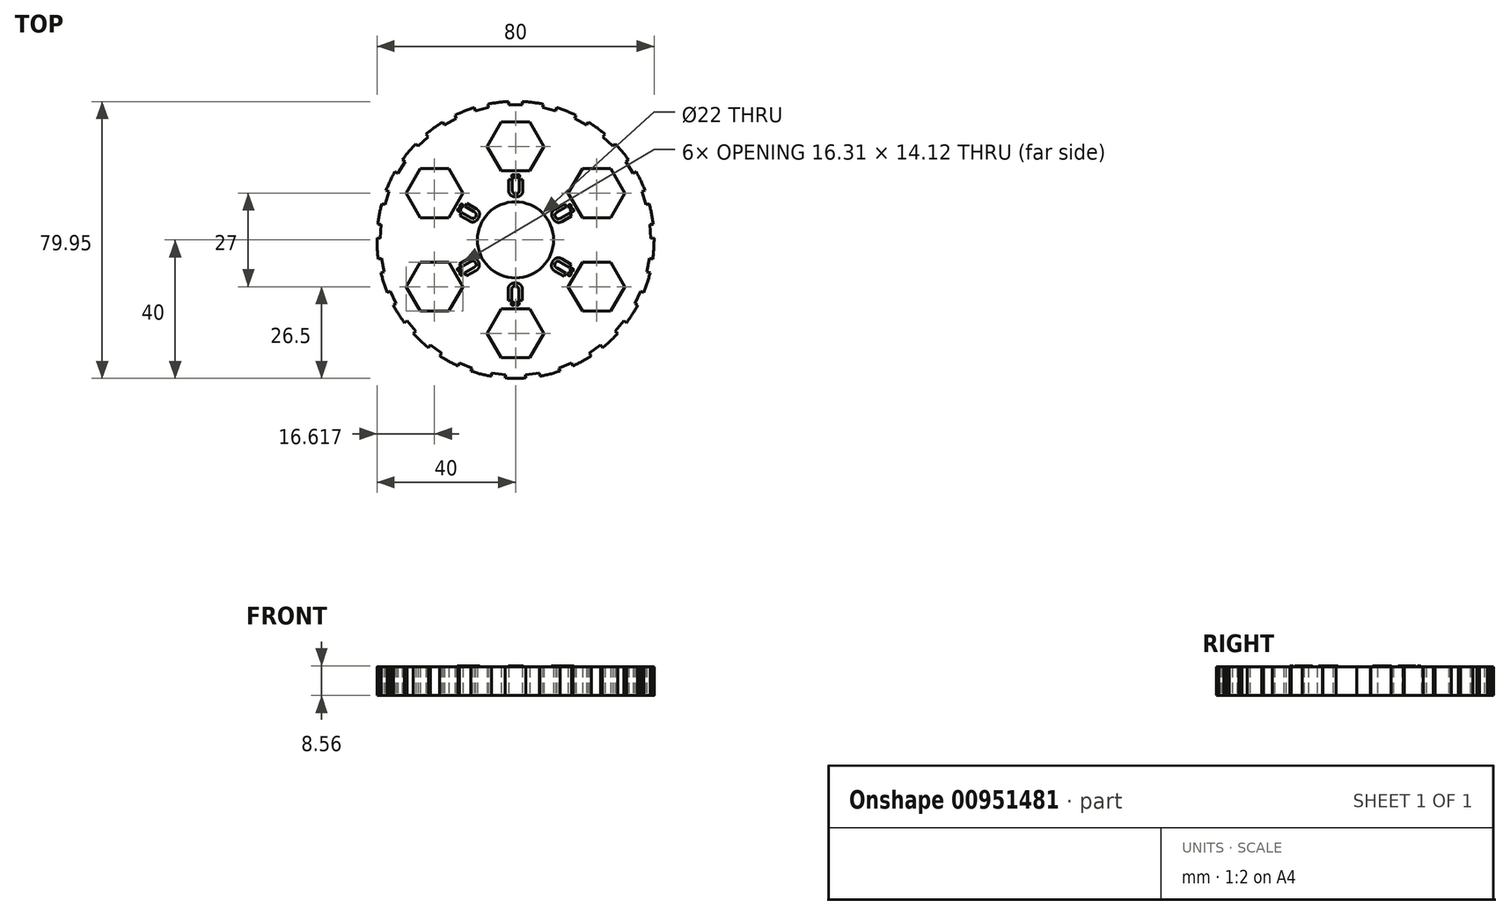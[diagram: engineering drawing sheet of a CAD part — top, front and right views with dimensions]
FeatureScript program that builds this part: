
annotation { "Feature Type Name" : "Feature", "Feature Type Description" : "" }
export const myFeature = defineFeature(function(context is Context, id is Id, definition is map)
    precondition{}
    {
        {
            var Q0;
            Q0=qCreatedBy(makeId("Top.planeOp"),FACE);
            var sketch = newSketch(context, id + "F0", { "sketchPlane" : qUnion([Q0])});
            skCircle(sketch, "E0", {"center": v(0, 0) * mm, "radius": 11 * mm});
            skCircle(sketch, "E1", {"center": v(0, 0) * mm, "radius": 40 * mm});
            skCircle(sketch, "E2.cCircle", {"center": v(0, 27) * mm, "radius": 7.06 * mm, "construction": true});
            skLineSegment(sketch, "E2.0", {"start": v(8.15, 27) * mm, "end": v(4.08, 19.94) * mm});
            skLineSegment(sketch, "E2.1", {"start": v(4.08, 19.94) * mm, "end": v(-4.08, 19.94) * mm});
            skLineSegment(sketch, "E2.2", {"start": v(-4.08, 19.94) * mm, "end": v(-8.15, 27) * mm});
            skLineSegment(sketch, "E2.3", {"start": v(-8.15, 27) * mm, "end": v(-4.08, 34.06) * mm});
            skLineSegment(sketch, "E2.4", {"start": v(-4.08, 34.06) * mm, "end": v(4.08, 34.06) * mm});
            skLineSegment(sketch, "E2.5", {"start": v(4.08, 34.06) * mm, "end": v(8.15, 27) * mm});
            skPoint(sketch, "E2.0.midPoint", {"position": v(6.12, 23.47) * mm});
            skLineSegment(sketch, "E3.1.0", {"start": v(-15.23, 13.5) * mm, "end": v(-19.3, 6.44) * mm});
            skLineSegment(sketch, "E3.1.1", {"start": v(-31.54, 13.5) * mm, "end": v(-27.46, 20.56) * mm});
            skLineSegment(sketch, "E3.1.2", {"start": v(-19.3, 6.44) * mm, "end": v(-27.46, 6.44) * mm});
            skLineSegment(sketch, "E3.1.3", {"start": v(-27.46, 20.56) * mm, "end": v(-19.3, 20.56) * mm});
            skLineSegment(sketch, "E3.1.4", {"start": v(-27.46, 6.44) * mm, "end": v(-31.54, 13.5) * mm});
            skLineSegment(sketch, "E3.1.5", {"start": v(-19.3, 20.56) * mm, "end": v(-15.23, 13.5) * mm});
            skPoint(sketch, "E3.1.6", {"position": v(-17.27, 17.03) * mm});
            skCircle(sketch, "E3.1.7", {"center": v(-23.38, 13.5) * mm, "radius": 7.06 * mm, "construction": true});
            skLineSegment(sketch, "E3.2.0", {"start": v(-19.3, -6.44) * mm, "end": v(-15.23, -13.5) * mm});
            skLineSegment(sketch, "E3.2.1", {"start": v(-27.46, -20.56) * mm, "end": v(-31.54, -13.5) * mm});
            skLineSegment(sketch, "E3.2.2", {"start": v(-15.23, -13.5) * mm, "end": v(-19.3, -20.56) * mm});
            skLineSegment(sketch, "E3.2.3", {"start": v(-31.54, -13.5) * mm, "end": v(-27.46, -6.44) * mm});
            skLineSegment(sketch, "E3.2.4", {"start": v(-19.3, -20.56) * mm, "end": v(-27.46, -20.56) * mm});
            skLineSegment(sketch, "E3.2.5", {"start": v(-27.46, -6.44) * mm, "end": v(-19.3, -6.44) * mm});
            skPoint(sketch, "E3.2.6", {"position": v(-23.38, -6.44) * mm});
            skCircle(sketch, "E3.2.7", {"center": v(-23.38, -13.5) * mm, "radius": 7.06 * mm, "construction": true});
            skLineSegment(sketch, "E3.3.0", {"start": v(-4.08, -19.94) * mm, "end": v(4.08, -19.94) * mm});
            skLineSegment(sketch, "E3.3.1", {"start": v(4.08, -34.06) * mm, "end": v(-4.08, -34.06) * mm});
            skLineSegment(sketch, "E3.3.2", {"start": v(4.08, -19.94) * mm, "end": v(8.15, -27) * mm});
            skLineSegment(sketch, "E3.3.3", {"start": v(-4.08, -34.06) * mm, "end": v(-8.15, -27) * mm});
            skLineSegment(sketch, "E3.3.4", {"start": v(8.15, -27) * mm, "end": v(4.08, -34.06) * mm});
            skLineSegment(sketch, "E3.3.5", {"start": v(-8.15, -27) * mm, "end": v(-4.08, -19.94) * mm});
            skPoint(sketch, "E3.3.6", {"position": v(-6.12, -23.47) * mm});
            skCircle(sketch, "E3.3.7", {"center": v(0, -27) * mm, "radius": 7.06 * mm, "construction": true});
            skLineSegment(sketch, "E3.4.0", {"start": v(15.23, -13.5) * mm, "end": v(19.3, -6.44) * mm});
            skLineSegment(sketch, "E3.4.1", {"start": v(31.54, -13.5) * mm, "end": v(27.46, -20.56) * mm});
            skLineSegment(sketch, "E3.4.2", {"start": v(19.3, -6.44) * mm, "end": v(27.46, -6.44) * mm});
            skLineSegment(sketch, "E3.4.3", {"start": v(27.46, -20.56) * mm, "end": v(19.3, -20.56) * mm});
            skLineSegment(sketch, "E3.4.4", {"start": v(27.46, -6.44) * mm, "end": v(31.54, -13.5) * mm});
            skLineSegment(sketch, "E3.4.5", {"start": v(19.3, -20.56) * mm, "end": v(15.23, -13.5) * mm});
            skPoint(sketch, "E3.4.6", {"position": v(17.27, -17.03) * mm});
            skCircle(sketch, "E3.4.7", {"center": v(23.38, -13.5) * mm, "radius": 7.06 * mm, "construction": true});
            skLineSegment(sketch, "E3.5.0", {"start": v(19.3, 6.44) * mm, "end": v(15.23, 13.5) * mm});
            skLineSegment(sketch, "E3.5.1", {"start": v(27.46, 20.56) * mm, "end": v(31.54, 13.5) * mm});
            skLineSegment(sketch, "E3.5.2", {"start": v(15.23, 13.5) * mm, "end": v(19.3, 20.56) * mm});
            skLineSegment(sketch, "E3.5.3", {"start": v(31.54, 13.5) * mm, "end": v(27.46, 6.44) * mm});
            skLineSegment(sketch, "E3.5.4", {"start": v(19.3, 20.56) * mm, "end": v(27.46, 20.56) * mm});
            skLineSegment(sketch, "E3.5.5", {"start": v(27.46, 6.44) * mm, "end": v(19.3, 6.44) * mm});
            skPoint(sketch, "E3.5.6", {"position": v(23.38, 6.44) * mm});
            skCircle(sketch, "E3.5.7", {"center": v(23.38, 13.5) * mm, "radius": 7.06 * mm, "construction": true});
            skLineSegment(sketch, "E4.bottom", {"start": v(2, 39) * mm, "end": v(-2, 39) * mm});
            skLineSegment(sketch, "E4.top", {"start": v(2, 41) * mm, "end": v(-2, 41) * mm});
            skLineSegment(sketch, "E4.left", {"start": v(2, 39) * mm, "end": v(2, 41) * mm});
            skLineSegment(sketch, "E4.right", {"start": v(-2, 39) * mm, "end": v(-2, 41) * mm});
            skPoint(sketch, "E4.middle", {"position": v(0, 40) * mm});
            skPoint(sketch, "E5.1.0", {"position": v(-9.95, 38.74) * mm});
            skLineSegment(sketch, "E5.1.1", {"start": v(-7.76, 38.27) * mm, "end": v(-11.64, 37.28) * mm});
            skLineSegment(sketch, "E5.1.2", {"start": v(-11.64, 37.28) * mm, "end": v(-12.13, 39.21) * mm});
            skLineSegment(sketch, "E5.1.3", {"start": v(-7.76, 38.27) * mm, "end": v(-8.26, 40.2) * mm});
            skLineSegment(sketch, "E5.1.4", {"start": v(-8.26, 40.2) * mm, "end": v(-12.13, 39.21) * mm});
            skPoint(sketch, "E5.2.0", {"position": v(-19.27, 35.05) * mm});
            skLineSegment(sketch, "E5.2.1", {"start": v(-17.04, 35.14) * mm, "end": v(-20.54, 33.21) * mm});
            skLineSegment(sketch, "E5.2.2", {"start": v(-20.54, 33.21) * mm, "end": v(-21.5, 34.97) * mm});
            skLineSegment(sketch, "E5.2.3", {"start": v(-17.04, 35.14) * mm, "end": v(-18, 36.9) * mm});
            skLineSegment(sketch, "E5.2.4", {"start": v(-18, 36.9) * mm, "end": v(-21.5, 34.97) * mm});
            skPoint(sketch, "E5.3.0", {"position": v(-27.38, 29.16) * mm});
            skLineSegment(sketch, "E5.3.1", {"start": v(-25.24, 29.8) * mm, "end": v(-28.16, 27.06) * mm});
            skLineSegment(sketch, "E5.3.2", {"start": v(-28.16, 27.06) * mm, "end": v(-29.52, 28.52) * mm});
            skLineSegment(sketch, "E5.3.3", {"start": v(-25.24, 29.8) * mm, "end": v(-26.6, 31.26) * mm});
            skLineSegment(sketch, "E5.3.4", {"start": v(-26.6, 31.26) * mm, "end": v(-29.52, 28.52) * mm});
            skPoint(sketch, "E5.4.0", {"position": v(-33.77, 21.43) * mm});
            skLineSegment(sketch, "E5.4.1", {"start": v(-31.86, 22.59) * mm, "end": v(-34, 19.2) * mm});
            skLineSegment(sketch, "E5.4.2", {"start": v(-34, 19.2) * mm, "end": v(-35.69, 20.28) * mm});
            skLineSegment(sketch, "E5.4.3", {"start": v(-31.86, 22.59) * mm, "end": v(-33.55, 23.66) * mm});
            skLineSegment(sketch, "E5.4.4", {"start": v(-33.55, 23.66) * mm, "end": v(-35.69, 20.28) * mm});
            skPoint(sketch, "E5.5.0", {"position": v(-38.04, 12.36) * mm});
            skLineSegment(sketch, "E5.5.1", {"start": v(-36.47, 13.95) * mm, "end": v(-37.7, 10.15) * mm});
            skLineSegment(sketch, "E5.5.2", {"start": v(-37.7, 10.15) * mm, "end": v(-39.61, 10.77) * mm});
            skLineSegment(sketch, "E5.5.3", {"start": v(-36.47, 13.95) * mm, "end": v(-38.38, 14.57) * mm});
            skLineSegment(sketch, "E5.5.4", {"start": v(-38.38, 14.57) * mm, "end": v(-39.61, 10.77) * mm});
            skPoint(sketch, "E5.6.0", {"position": v(-39.92, 2.51) * mm});
            skLineSegment(sketch, "E5.6.1", {"start": v(-38.8, 4.44) * mm, "end": v(-39.05, 0.45) * mm});
            skLineSegment(sketch, "E5.6.2", {"start": v(-39.05, 0.45) * mm, "end": v(-41.04, 0.58) * mm});
            skLineSegment(sketch, "E5.6.3", {"start": v(-38.8, 4.44) * mm, "end": v(-40.8, 4.57) * mm});
            skLineSegment(sketch, "E5.6.4", {"start": v(-40.8, 4.57) * mm, "end": v(-41.04, 0.58) * mm});
            skPoint(sketch, "E5.7.0", {"position": v(-39.3, -7.5) * mm});
            skLineSegment(sketch, "E5.7.1", {"start": v(-38.68, -5.34) * mm, "end": v(-37.93, -9.27) * mm});
            skLineSegment(sketch, "E5.7.2", {"start": v(-37.93, -9.27) * mm, "end": v(-39.9, -9.65) * mm});
            skLineSegment(sketch, "E5.7.3", {"start": v(-38.68, -5.34) * mm, "end": v(-40.65, -5.72) * mm});
            skLineSegment(sketch, "E5.7.4", {"start": v(-40.65, -5.72) * mm, "end": v(-39.9, -9.65) * mm});
            skPoint(sketch, "E5.8.0", {"position": v(-36.2, -17.03) * mm});
            skLineSegment(sketch, "E5.8.1", {"start": v(-36.14, -14.8) * mm, "end": v(-34.44, -18.42) * mm});
            skLineSegment(sketch, "E5.8.2", {"start": v(-34.44, -18.42) * mm, "end": v(-36.25, -19.27) * mm});
            skLineSegment(sketch, "E5.8.3", {"start": v(-36.14, -14.8) * mm, "end": v(-37.95, -15.65) * mm});
            skLineSegment(sketch, "E5.8.4", {"start": v(-37.95, -15.65) * mm, "end": v(-36.25, -19.27) * mm});
            skPoint(sketch, "E5.9.0", {"position": v(-30.82, -25.5) * mm});
            skLineSegment(sketch, "E5.9.1", {"start": v(-31.32, -23.32) * mm, "end": v(-28.78, -26.4) * mm});
            skLineSegment(sketch, "E5.9.2", {"start": v(-28.78, -26.4) * mm, "end": v(-30.32, -27.68) * mm});
            skLineSegment(sketch, "E5.9.3", {"start": v(-31.32, -23.32) * mm, "end": v(-32.87, -24.6) * mm});
            skLineSegment(sketch, "E5.9.4", {"start": v(-32.87, -24.6) * mm, "end": v(-30.32, -27.68) * mm});
            skPoint(sketch, "E5.10.0", {"position": v(-23.51, -32.36) * mm});
            skLineSegment(sketch, "E5.10.1", {"start": v(-24.54, -30.38) * mm, "end": v(-21.3, -32.73) * mm});
            skLineSegment(sketch, "E5.10.2", {"start": v(-21.3, -32.73) * mm, "end": v(-22.48, -34.35) * mm});
            skLineSegment(sketch, "E5.10.3", {"start": v(-24.54, -30.38) * mm, "end": v(-25.72, -32) * mm});
            skLineSegment(sketch, "E5.10.4", {"start": v(-25.72, -32) * mm, "end": v(-22.48, -34.35) * mm});
            skPoint(sketch, "E5.11.0", {"position": v(-14.72, -37.2) * mm});
            skLineSegment(sketch, "E5.11.1", {"start": v(-16.22, -35.53) * mm, "end": v(-12.5, -37) * mm});
            skLineSegment(sketch, "E5.11.2", {"start": v(-12.5, -37) * mm, "end": v(-13.23, -38.86) * mm});
            skLineSegment(sketch, "E5.11.3", {"start": v(-16.22, -35.53) * mm, "end": v(-16.95, -37.38) * mm});
            skLineSegment(sketch, "E5.11.4", {"start": v(-16.95, -37.38) * mm, "end": v(-13.23, -38.86) * mm});
            skPoint(sketch, "E5.12.0", {"position": v(-5.01, -39.68) * mm});
            skLineSegment(sketch, "E5.12.1", {"start": v(-6.87, -38.44) * mm, "end": v(-2.9, -38.94) * mm});
            skLineSegment(sketch, "E5.12.2", {"start": v(-2.9, -38.94) * mm, "end": v(-3.15, -40.93) * mm});
            skLineSegment(sketch, "E5.12.3", {"start": v(-6.87, -38.44) * mm, "end": v(-7.12, -40.43) * mm});
            skLineSegment(sketch, "E5.12.4", {"start": v(-7.12, -40.43) * mm, "end": v(-3.15, -40.93) * mm});
            skPoint(sketch, "E5.13.0", {"position": v(5.01, -39.68) * mm});
            skLineSegment(sketch, "E5.13.1", {"start": v(2.9, -38.94) * mm, "end": v(6.87, -38.44) * mm});
            skLineSegment(sketch, "E5.13.2", {"start": v(6.87, -38.44) * mm, "end": v(7.12, -40.43) * mm});
            skLineSegment(sketch, "E5.13.3", {"start": v(2.9, -38.94) * mm, "end": v(3.15, -40.93) * mm});
            skLineSegment(sketch, "E5.13.4", {"start": v(3.15, -40.93) * mm, "end": v(7.12, -40.43) * mm});
            skPoint(sketch, "E5.14.0", {"position": v(14.72, -37.2) * mm});
            skLineSegment(sketch, "E5.14.1", {"start": v(12.5, -37) * mm, "end": v(16.22, -35.53) * mm});
            skLineSegment(sketch, "E5.14.2", {"start": v(16.22, -35.53) * mm, "end": v(16.95, -37.38) * mm});
            skLineSegment(sketch, "E5.14.3", {"start": v(12.5, -37) * mm, "end": v(13.23, -38.86) * mm});
            skLineSegment(sketch, "E5.14.4", {"start": v(13.23, -38.86) * mm, "end": v(16.95, -37.38) * mm});
            skPoint(sketch, "E5.15.0", {"position": v(23.51, -32.36) * mm});
            skLineSegment(sketch, "E5.15.1", {"start": v(21.3, -32.73) * mm, "end": v(24.54, -30.38) * mm});
            skLineSegment(sketch, "E5.15.2", {"start": v(24.54, -30.38) * mm, "end": v(25.72, -32) * mm});
            skLineSegment(sketch, "E5.15.3", {"start": v(21.3, -32.73) * mm, "end": v(22.48, -34.35) * mm});
            skLineSegment(sketch, "E5.15.4", {"start": v(22.48, -34.35) * mm, "end": v(25.72, -32) * mm});
            skPoint(sketch, "E5.16.0", {"position": v(30.82, -25.5) * mm});
            skLineSegment(sketch, "E5.16.1", {"start": v(28.78, -26.4) * mm, "end": v(31.32, -23.32) * mm});
            skLineSegment(sketch, "E5.16.2", {"start": v(31.32, -23.32) * mm, "end": v(32.87, -24.6) * mm});
            skLineSegment(sketch, "E5.16.3", {"start": v(28.78, -26.4) * mm, "end": v(30.32, -27.68) * mm});
            skLineSegment(sketch, "E5.16.4", {"start": v(30.32, -27.68) * mm, "end": v(32.87, -24.6) * mm});
            skPoint(sketch, "E5.17.0", {"position": v(36.2, -17.03) * mm});
            skLineSegment(sketch, "E5.17.1", {"start": v(34.44, -18.42) * mm, "end": v(36.14, -14.8) * mm});
            skLineSegment(sketch, "E5.17.2", {"start": v(36.14, -14.8) * mm, "end": v(37.95, -15.65) * mm});
            skLineSegment(sketch, "E5.17.3", {"start": v(34.44, -18.42) * mm, "end": v(36.25, -19.27) * mm});
            skLineSegment(sketch, "E5.17.4", {"start": v(36.25, -19.27) * mm, "end": v(37.95, -15.65) * mm});
            skPoint(sketch, "E5.18.0", {"position": v(39.3, -7.5) * mm});
            skLineSegment(sketch, "E5.18.1", {"start": v(37.93, -9.27) * mm, "end": v(38.68, -5.34) * mm});
            skLineSegment(sketch, "E5.18.2", {"start": v(38.68, -5.34) * mm, "end": v(40.65, -5.72) * mm});
            skLineSegment(sketch, "E5.18.3", {"start": v(37.93, -9.27) * mm, "end": v(39.9, -9.65) * mm});
            skLineSegment(sketch, "E5.18.4", {"start": v(39.9, -9.65) * mm, "end": v(40.65, -5.72) * mm});
            skPoint(sketch, "E5.19.0", {"position": v(39.92, 2.51) * mm});
            skLineSegment(sketch, "E5.19.1", {"start": v(39.05, 0.45) * mm, "end": v(38.8, 4.44) * mm});
            skLineSegment(sketch, "E5.19.2", {"start": v(38.8, 4.44) * mm, "end": v(40.8, 4.57) * mm});
            skLineSegment(sketch, "E5.19.3", {"start": v(39.05, 0.45) * mm, "end": v(41.04, 0.58) * mm});
            skLineSegment(sketch, "E5.19.4", {"start": v(41.04, 0.58) * mm, "end": v(40.8, 4.57) * mm});
            skPoint(sketch, "E5.20.0", {"position": v(38.04, 12.36) * mm});
            skLineSegment(sketch, "E5.20.1", {"start": v(37.7, 10.15) * mm, "end": v(36.47, 13.95) * mm});
            skLineSegment(sketch, "E5.20.2", {"start": v(36.47, 13.95) * mm, "end": v(38.38, 14.57) * mm});
            skLineSegment(sketch, "E5.20.3", {"start": v(37.7, 10.15) * mm, "end": v(39.61, 10.77) * mm});
            skLineSegment(sketch, "E5.20.4", {"start": v(39.61, 10.77) * mm, "end": v(38.38, 14.57) * mm});
            skPoint(sketch, "E5.21.0", {"position": v(33.77, 21.43) * mm});
            skLineSegment(sketch, "E5.21.1", {"start": v(34, 19.2) * mm, "end": v(31.86, 22.59) * mm});
            skLineSegment(sketch, "E5.21.2", {"start": v(31.86, 22.59) * mm, "end": v(33.55, 23.66) * mm});
            skLineSegment(sketch, "E5.21.3", {"start": v(34, 19.2) * mm, "end": v(35.69, 20.28) * mm});
            skLineSegment(sketch, "E5.21.4", {"start": v(35.69, 20.28) * mm, "end": v(33.55, 23.66) * mm});
            skPoint(sketch, "E5.22.0", {"position": v(27.38, 29.16) * mm});
            skLineSegment(sketch, "E5.22.1", {"start": v(28.16, 27.06) * mm, "end": v(25.24, 29.8) * mm});
            skLineSegment(sketch, "E5.22.2", {"start": v(25.24, 29.8) * mm, "end": v(26.6, 31.26) * mm});
            skLineSegment(sketch, "E5.22.3", {"start": v(28.16, 27.06) * mm, "end": v(29.52, 28.52) * mm});
            skLineSegment(sketch, "E5.22.4", {"start": v(29.52, 28.52) * mm, "end": v(26.6, 31.26) * mm});
            skPoint(sketch, "E5.23.0", {"position": v(19.27, 35.05) * mm});
            skLineSegment(sketch, "E5.23.1", {"start": v(20.54, 33.21) * mm, "end": v(17.04, 35.14) * mm});
            skLineSegment(sketch, "E5.23.2", {"start": v(17.04, 35.14) * mm, "end": v(18, 36.9) * mm});
            skLineSegment(sketch, "E5.23.3", {"start": v(20.54, 33.21) * mm, "end": v(21.5, 34.97) * mm});
            skLineSegment(sketch, "E5.23.4", {"start": v(21.5, 34.97) * mm, "end": v(18, 36.9) * mm});
            skPoint(sketch, "E5.24.0", {"position": v(9.95, 38.74) * mm});
            skLineSegment(sketch, "E5.24.1", {"start": v(11.64, 37.28) * mm, "end": v(7.76, 38.27) * mm});
            skLineSegment(sketch, "E5.24.2", {"start": v(7.76, 38.27) * mm, "end": v(8.26, 40.2) * mm});
            skLineSegment(sketch, "E5.24.3", {"start": v(11.64, 37.28) * mm, "end": v(12.13, 39.21) * mm});
            skLineSegment(sketch, "E5.24.4", {"start": v(12.13, 39.21) * mm, "end": v(8.26, 40.2) * mm});
            skLineSegment(sketch, "E6", {"start": v(0, 11) * mm, "end": v(0, -11) * mm, "construction": true});
            skLineSegment(sketch, "E7", {"start": v(-11, 0) * mm, "end": v(11, 0) * mm, "construction": true});
            skSolve(sketch);
        }
        {
            var Q0;
            Q0=makeQuery(id+"F0.imprint","IMPRINT",FACE,{"disambiguationData":[TD([[makeQuery(id+"F0.imprint","IMPRINT",EDGE,{"derivedFrom":sQuery(id+"F0.wireOp",EDGE,"E0")}),-1.0]])]});
            var Q1;
            Q1=makeQuery(id+"F0.imprint","IMPRINT",FACE,{"disambiguationData":[TD([[makeQuery(id+"F0.imprint","IMPRINT",EDGE,{"derivedFrom":sQuery(id+"F0.wireOp",EDGE,"70343d24-3078-4203-b73a-85bb35b72b07.sketch_text.stroke-15")}),-1.0]])]});
            var Q2;
            Q2=makeQuery(id+"F0.imprint","IMPRINT",FACE,{"disambiguationData":[TD([[makeQuery(id+"F0.imprint","IMPRINT",EDGE,{"derivedFrom":sQuery(id+"F0.wireOp",EDGE,"70343d24-3078-4203-b73a-85bb35b72b07.sketch_text.stroke-23")}),-1.0]])]});
            var Q3;
            Q3=makeQuery(id+"F0.imprint","IMPRINT",FACE,{"disambiguationData":[TD([[makeQuery(id+"F0.imprint","IMPRINT",EDGE,{"derivedFrom":sQuery(id+"F0.wireOp",EDGE,"70343d24-3078-4203-b73a-85bb35b72b07.sketch_text.stroke-0")}),-1.0]])]});
            extrude(context, id + "F1", {"entities" : qUnion([Q0, Q1, Q2, Q3]), "depth" : 8.25 * mm, "offsetDistance" : 25 * mm});
        }
        {
            var Q0;
            Q0=makeQuery(id+"F1.opExtrude","CAP_FACE",FACE,{"disambiguationData":[OSD([sQuery(id+"F0.wireOp",EDGE,"E0"),sQuery(id+"F0.wireOp",EDGE,"E1"),sQuery(id+"F0.wireOp",EDGE,"E2.0"),sQuery(id+"F0.wireOp",EDGE,"E2.1"),sQuery(id+"F0.wireOp",EDGE,"E2.2"),sQuery(id+"F0.wireOp",EDGE,"E2.3"),sQuery(id+"F0.wireOp",EDGE,"E2.4"),sQuery(id+"F0.wireOp",EDGE,"E2.5"),sQuery(id+"F0.wireOp",EDGE,"E3.1.0"),sQuery(id+"F0.wireOp",EDGE,"E3.1.1"),sQuery(id+"F0.wireOp",EDGE,"E3.1.2"),sQuery(id+"F0.wireOp",EDGE,"E3.1.3"),sQuery(id+"F0.wireOp",EDGE,"E3.1.4"),sQuery(id+"F0.wireOp",EDGE,"E3.1.5"),sQuery(id+"F0.wireOp",EDGE,"E3.2.0"),sQuery(id+"F0.wireOp",EDGE,"E3.2.1"),sQuery(id+"F0.wireOp",EDGE,"E3.2.2"),sQuery(id+"F0.wireOp",EDGE,"E3.2.3"),sQuery(id+"F0.wireOp",EDGE,"E3.2.4"),sQuery(id+"F0.wireOp",EDGE,"E3.2.5"),sQuery(id+"F0.wireOp",EDGE,"E3.3.0"),sQuery(id+"F0.wireOp",EDGE,"E3.3.1"),sQuery(id+"F0.wireOp",EDGE,"E3.3.2"),sQuery(id+"F0.wireOp",EDGE,"E3.3.3"),sQuery(id+"F0.wireOp",EDGE,"E3.3.4"),sQuery(id+"F0.wireOp",EDGE,"E3.3.5"),sQuery(id+"F0.wireOp",EDGE,"E3.4.0"),sQuery(id+"F0.wireOp",EDGE,"E3.4.1"),sQuery(id+"F0.wireOp",EDGE,"E3.4.2"),sQuery(id+"F0.wireOp",EDGE,"E3.4.3"),sQuery(id+"F0.wireOp",EDGE,"E3.4.4"),sQuery(id+"F0.wireOp",EDGE,"E3.4.5"),sQuery(id+"F0.wireOp",EDGE,"E3.5.0"),sQuery(id+"F0.wireOp",EDGE,"E3.5.1"),sQuery(id+"F0.wireOp",EDGE,"E3.5.2"),sQuery(id+"F0.wireOp",EDGE,"E3.5.3"),sQuery(id+"F0.wireOp",EDGE,"E3.5.4"),sQuery(id+"F0.wireOp",EDGE,"E3.5.5"),sQuery(id+"F0.wireOp",EDGE,"E4.bottom"),sQuery(id+"F0.wireOp",EDGE,"E4.left"),sQuery(id+"F0.wireOp",EDGE,"E4.right"),sQuery(id+"F0.wireOp",EDGE,"E5.1.1"),sQuery(id+"F0.wireOp",EDGE,"E5.1.2"),sQuery(id+"F0.wireOp",EDGE,"E5.1.3"),sQuery(id+"F0.wireOp",EDGE,"E5.2.1"),sQuery(id+"F0.wireOp",EDGE,"E5.2.2"),sQuery(id+"F0.wireOp",EDGE,"E5.2.3"),sQuery(id+"F0.wireOp",EDGE,"E5.3.1"),sQuery(id+"F0.wireOp",EDGE,"E5.3.2"),sQuery(id+"F0.wireOp",EDGE,"E5.3.3"),sQuery(id+"F0.wireOp",EDGE,"E5.4.1"),sQuery(id+"F0.wireOp",EDGE,"E5.4.2"),sQuery(id+"F0.wireOp",EDGE,"E5.4.3"),sQuery(id+"F0.wireOp",EDGE,"E5.5.1"),sQuery(id+"F0.wireOp",EDGE,"E5.5.2"),sQuery(id+"F0.wireOp",EDGE,"E5.5.3"),sQuery(id+"F0.wireOp",EDGE,"E5.6.1"),sQuery(id+"F0.wireOp",EDGE,"E5.6.2"),sQuery(id+"F0.wireOp",EDGE,"E5.6.3"),sQuery(id+"F0.wireOp",EDGE,"E5.7.1"),sQuery(id+"F0.wireOp",EDGE,"E5.7.2"),sQuery(id+"F0.wireOp",EDGE,"E5.7.3"),sQuery(id+"F0.wireOp",EDGE,"E5.8.1"),sQuery(id+"F0.wireOp",EDGE,"E5.8.2"),sQuery(id+"F0.wireOp",EDGE,"E5.8.3"),sQuery(id+"F0.wireOp",EDGE,"E5.9.1"),sQuery(id+"F0.wireOp",EDGE,"E5.9.2"),sQuery(id+"F0.wireOp",EDGE,"E5.9.3"),sQuery(id+"F0.wireOp",EDGE,"E5.10.1"),sQuery(id+"F0.wireOp",EDGE,"E5.10.2"),sQuery(id+"F0.wireOp",EDGE,"E5.10.3"),sQuery(id+"F0.wireOp",EDGE,"E5.11.1"),sQuery(id+"F0.wireOp",EDGE,"E5.11.2"),sQuery(id+"F0.wireOp",EDGE,"E5.11.3"),sQuery(id+"F0.wireOp",EDGE,"E5.12.1"),sQuery(id+"F0.wireOp",EDGE,"E5.12.2"),sQuery(id+"F0.wireOp",EDGE,"E5.12.3"),sQuery(id+"F0.wireOp",EDGE,"E5.13.1"),sQuery(id+"F0.wireOp",EDGE,"E5.13.2"),sQuery(id+"F0.wireOp",EDGE,"E5.13.3"),sQuery(id+"F0.wireOp",EDGE,"E5.14.1"),sQuery(id+"F0.wireOp",EDGE,"E5.14.2"),sQuery(id+"F0.wireOp",EDGE,"E5.14.3"),sQuery(id+"F0.wireOp",EDGE,"E5.15.1"),sQuery(id+"F0.wireOp",EDGE,"E5.15.2"),sQuery(id+"F0.wireOp",EDGE,"E5.15.3"),sQuery(id+"F0.wireOp",EDGE,"E5.16.1"),sQuery(id+"F0.wireOp",EDGE,"E5.16.2"),sQuery(id+"F0.wireOp",EDGE,"E5.16.3"),sQuery(id+"F0.wireOp",EDGE,"E5.17.1"),sQuery(id+"F0.wireOp",EDGE,"E5.17.2"),sQuery(id+"F0.wireOp",EDGE,"E5.17.3"),sQuery(id+"F0.wireOp",EDGE,"E5.18.1"),sQuery(id+"F0.wireOp",EDGE,"E5.18.2"),sQuery(id+"F0.wireOp",EDGE,"E5.18.3"),sQuery(id+"F0.wireOp",EDGE,"E5.19.1"),sQuery(id+"F0.wireOp",EDGE,"E5.19.2"),sQuery(id+"F0.wireOp",EDGE,"E5.19.3"),sQuery(id+"F0.wireOp",EDGE,"E5.20.1"),sQuery(id+"F0.wireOp",EDGE,"E5.20.2"),sQuery(id+"F0.wireOp",EDGE,"E5.20.3"),sQuery(id+"F0.wireOp",EDGE,"E5.21.1"),sQuery(id+"F0.wireOp",EDGE,"E5.21.2"),sQuery(id+"F0.wireOp",EDGE,"E5.21.3"),sQuery(id+"F0.wireOp",EDGE,"E5.22.1"),sQuery(id+"F0.wireOp",EDGE,"E5.22.2"),sQuery(id+"F0.wireOp",EDGE,"E5.22.3"),sQuery(id+"F0.wireOp",EDGE,"E5.23.1"),sQuery(id+"F0.wireOp",EDGE,"E5.23.2"),sQuery(id+"F0.wireOp",EDGE,"E5.23.3"),sQuery(id+"F0.wireOp",EDGE,"E5.24.1"),sQuery(id+"F0.wireOp",EDGE,"E5.24.2"),sQuery(id+"F0.wireOp",EDGE,"E5.24.3")])],"isStart":false});
            var sketch = newSketch(context, id + "F2", { "sketchPlane" : qUnion([Q0])});
            skText(sketch, "E8", { "text": "Ü", "fontName": "OpenSans-Bold.ttf"});
            const initialGuessF2  = {"E8": [-0.00255, 0.0125, 1, 0, 0.005]};
            skSetInitialGuess(sketch, initialGuessF2);
            skSolve(sketch);
        }
        {
            var Q0;
            Q0 = qSketchRegion(id + "F2", true);
            extrude(context, id + "F3", {"entities" : qUnion([Q0]), "depth" : 0.3 * mm, "offsetDistance" : 25 * mm});
        }
        {
            var Q0;
            Q0=qCreatedBy(makeId("Front.planeOp"),FACE);
            var sketch = newSketch(context, id + "F4", { "sketchPlane" : qUnion([Q0])});
            skLineSegment(sketch, "E9", {"start": v(0, 12.93) * mm, "end": v(0, -12.56) * mm, "construction": true});
            skSolve(sketch);
        }
        {
            var Q0;
            Q0=makeQuery(id+"F3.opExtrude","SWEPT_BODY",BODY,{"disambiguationData":[OSD([sQuery(id+"F2.wireOp",EDGE,"E8.sketch_text.stroke-0"),sQuery(id+"F2.wireOp",EDGE,"E8.sketch_text.stroke-1"),sQuery(id+"F2.wireOp",EDGE,"E8.sketch_text.stroke-2"),sQuery(id+"F2.wireOp",EDGE,"E8.sketch_text.stroke-3"),sQuery(id+"F2.wireOp",EDGE,"E8.sketch_text.stroke-4"),sQuery(id+"F2.wireOp",EDGE,"E8.sketch_text.stroke-5"),sQuery(id+"F2.wireOp",EDGE,"E8.sketch_text.stroke-6"),sQuery(id+"F2.wireOp",EDGE,"E8.sketch_text.stroke-7"),sQuery(id+"F2.wireOp",EDGE,"E8.sketch_text.stroke-8"),sQuery(id+"F2.wireOp",EDGE,"E8.sketch_text.stroke-9"),sQuery(id+"F2.wireOp",EDGE,"E8.sketch_text.stroke-10"),sQuery(id+"F2.wireOp",EDGE,"E8.sketch_text.stroke-11"),sQuery(id+"F2.wireOp",EDGE,"E8.sketch_text.stroke-12"),sQuery(id+"F2.wireOp",EDGE,"E8.sketch_text.stroke-13"),sQuery(id+"F2.wireOp",EDGE,"E8.sketch_text.stroke-14")])]});
            var Q1;
            Q1=makeQuery(id+"F3.opExtrude","SWEPT_BODY",BODY,{"disambiguationData":[OSD([sQuery(id+"F2.wireOp",EDGE,"E8.sketch_text.stroke-15"),sQuery(id+"F2.wireOp",EDGE,"E8.sketch_text.stroke-16"),sQuery(id+"F2.wireOp",EDGE,"E8.sketch_text.stroke-17"),sQuery(id+"F2.wireOp",EDGE,"E8.sketch_text.stroke-18"),sQuery(id+"F2.wireOp",EDGE,"E8.sketch_text.stroke-19"),sQuery(id+"F2.wireOp",EDGE,"E8.sketch_text.stroke-20"),sQuery(id+"F2.wireOp",EDGE,"E8.sketch_text.stroke-21"),sQuery(id+"F2.wireOp",EDGE,"E8.sketch_text.stroke-22")])]});
            var Q2;
            Q2=makeQuery(id+"F3.opExtrude","SWEPT_BODY",BODY,{"disambiguationData":[OSD([sQuery(id+"F2.wireOp",EDGE,"E8.sketch_text.stroke-23"),sQuery(id+"F2.wireOp",EDGE,"E8.sketch_text.stroke-24"),sQuery(id+"F2.wireOp",EDGE,"E8.sketch_text.stroke-25"),sQuery(id+"F2.wireOp",EDGE,"E8.sketch_text.stroke-26"),sQuery(id+"F2.wireOp",EDGE,"E8.sketch_text.stroke-27"),sQuery(id+"F2.wireOp",EDGE,"E8.sketch_text.stroke-28"),sQuery(id+"F2.wireOp",EDGE,"E8.sketch_text.stroke-29"),sQuery(id+"F2.wireOp",EDGE,"E8.sketch_text.stroke-30")])]});
            var Q3;
            Q3=sQuery(id+"F4.wireOp",EDGE,"E9");
            circularPattern(context, id + "F5", {"entities" : qUnion([Q0, Q1, Q2]), "axis" : qUnion([Q3]), "angle" : 360 * degree, "instanceCount" : 6, "equalSpace" : true});
        }
    });
